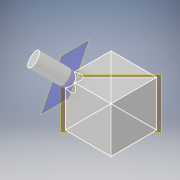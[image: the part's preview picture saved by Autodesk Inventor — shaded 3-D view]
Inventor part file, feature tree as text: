
AUTODESK INVENTOR PART (.ipt)
format: ipt  version: 2019 (Build 230136000, 136)  size: 117,760 bytes
history: native  units: mm
features: plane x3, sketch x3, extrude x2, projected_geometry x2
ambient origin geometry x8: Origin, YZ Plane, XZ Plane, XY Plane, X Axis, Y Axis, Z Axis, Center Point
bodies: Solid1 (feature_tree)
feature tree (10):
  extrude  "Extrusion1"  Depth=25.0mm
  plane  "Work Plane2"
  sketch  "Sketch2"  dims[d2=25.0mm d3=0.0mm d4=8.0mm]
  plane  "Work Plane3"
  extrude  "Extrusion2"  Depth=25.0mm
  sketch  "Sketch1"  dims[d0=25.0mm d1=25.0mm]
  plane  "Work Plane1"
  projected_geometry  "Projected Loop1"
  projected_geometry  "Projected Loop2"
  sketch  "Sketch3"  dims[d5=10.0mm d6=15.0mm d7=0.0mm d8=0.0mm]
